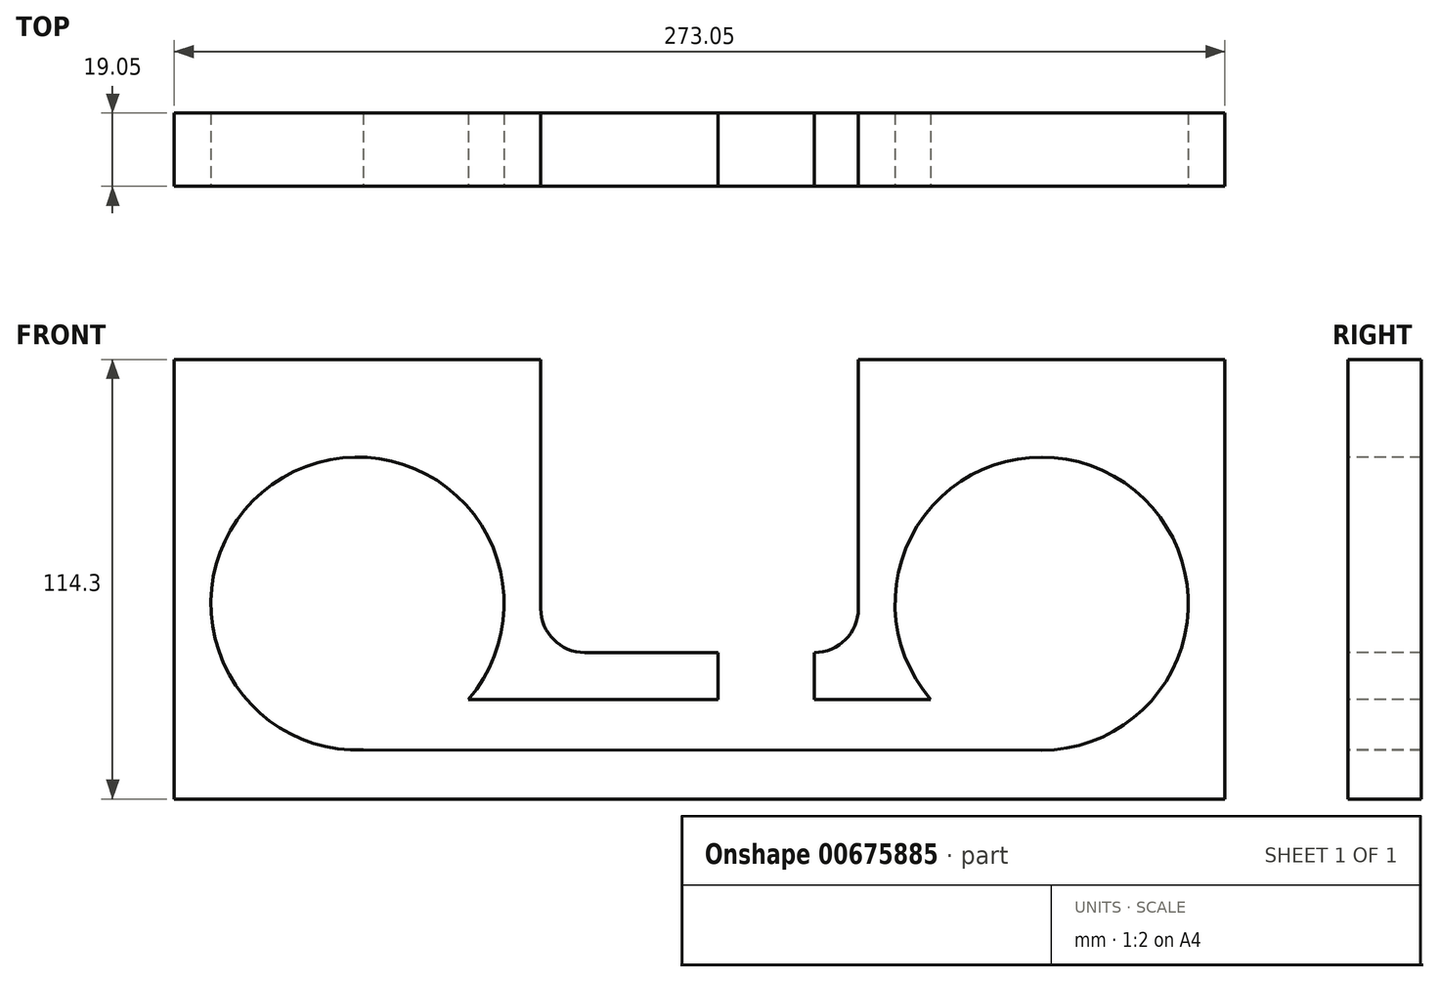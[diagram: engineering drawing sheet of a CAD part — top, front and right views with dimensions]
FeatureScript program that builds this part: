
annotation { "Feature Type Name" : "Feature", "Feature Type Description" : "" }
export const myFeature = defineFeature(function(context is Context, id is Id, definition is map)
    precondition{}
    {
        {
            var Q0;
            Q0=qCreatedBy(makeId("Front.planeOp"),FACE);
            var sketch = newSketch(context, id + "F0", { "sketchPlane" : qUnion([Q0])});
            skLineSegment(sketch, "E0.bottom", {"start": v(0, 0) * mm, "end": v(273.05, 0) * mm});
            skLineSegment(sketch, "E0.top", {"start": v(0, 114.3) * mm, "end": v(273.05, 114.3) * mm});
            skLineSegment(sketch, "E0.left", {"start": v(0, 0) * mm, "end": v(0, 114.3) * mm});
            skLineSegment(sketch, "E0.right", {"start": v(273.05, 0) * mm, "end": v(273.05, 114.3) * mm});
            skSolve(sketch);
        }
        {
            var Q0;
            Q0=makeQuery(id+"F0.imprint","IMPRINT",FACE,{"disambiguationData":[TD([[makeQuery(id+"F0.imprint","IMPRINT",EDGE,{"derivedFrom":sQuery(id+"F0.wireOp",EDGE,"E0.bottom")}),1.0]])]});
            extrude(context, id + "F1", {"entities" : qUnion([Q0]), "depth" : 19.05 * mm, "offsetDistance" : 25.4 * mm});
        }
        {
            var Q0;
            Q0=makeQuery(id+"F1.opExtrude","CAP_FACE",FACE,{"disambiguationData":[OSD([sQuery(id+"F0.wireOp",EDGE,"E0.bottom"),sQuery(id+"F0.wireOp",EDGE,"E0.top"),sQuery(id+"F0.wireOp",EDGE,"E0.left"),sQuery(id+"F0.wireOp",EDGE,"E0.right")])],"isStart":false});
            var sketch = newSketch(context, id + "F2", { "sketchPlane" : qUnion([Q0])});
            skCircle(sketch, "E1", {"center": v(47.63, 50.8) * mm, "radius": 38.1 * mm});
            skCircle(sketch, "E2", {"center": v(225.43, 50.8) * mm, "radius": 38.1 * mm});
            skSolve(sketch);
        }
        {
            var Q0;
            Q0=makeQuery(id+"F2.imprint","IMPRINT",FACE,{"disambiguationData":[TD([[makeQuery(id+"F2.imprint","IMPRINT",EDGE,{"derivedFrom":sQuery(id+"F2.wireOp",EDGE,"E1")}),1.0]])]});
            var Q1;
            Q1=makeQuery(id+"F2.imprint","IMPRINT",FACE,{"disambiguationData":[TD([[makeQuery(id+"F2.imprint","IMPRINT",EDGE,{"derivedFrom":sQuery(id+"F2.wireOp",EDGE,"E2")}),1.0]])]});
            extrude(context, id + "F3", {"entities" : qUnion([Q0, Q1]), "operationType" : NewBodyOperationType.REMOVE, "oppositeDirection" : true, "depth" : 25.4 * mm, "offsetDistance" : 25.4 * mm});
        }
        {
            var Q0;
            Q0=makeQuery(id+"F1.opExtrude","CAP_FACE",FACE,{"disambiguationData":[OSD([sQuery(id+"F0.wireOp",EDGE,"E0.bottom"),sQuery(id+"F0.wireOp",EDGE,"E0.top"),sQuery(id+"F0.wireOp",EDGE,"E0.left"),sQuery(id+"F0.wireOp",EDGE,"E0.right")])],"isStart":false});
            var sketch = newSketch(context, id + "F4", { "sketchPlane" : qUnion([Q0])});
            skLineSegment(sketch, "E3", {"start": v(95.25, 114.3) * mm, "end": v(95.25, 49.53) * mm});
            skLineSegment(sketch, "E4", {"start": v(106.68, 38.1) * mm, "end": v(166.37, 38.1) * mm});
            skLineSegment(sketch, "E5", {"start": v(177.8, 49.53) * mm, "end": v(177.8, 114.3) * mm});
            skPoint(sketch, "E6.visualSharp", {"position": v(95.25, 38.1) * mm});
            skArc(sketch, "E6.filletArc", {"start": v(95.25, 49.53) * mm, "mid": v(98.6, 41.45) * mm, "end": v(106.68, 38.1) * mm});
            skPoint(sketch, "E7.visualSharp", {"position": v(177.8, 38.1) * mm});
            skArc(sketch, "E7.filletArc", {"start": v(166.37, 38.1) * mm, "mid": v(174.45, 41.45) * mm, "end": v(177.8, 49.53) * mm});
            skSolve(sketch);
        }
        {
            var Q0;
            {var subQ1=sQuery(id+"F4.wireOp",EDGE,"E3");Q0=makeQuery(id+"F4.imprint","IMPRINT",FACE,{"disambiguationData":[TD([[makeQuery(id+"F4.imprint","IMPRINT",EDGE,{"derivedFrom":subQ1}),1.0]])]});}
            extrude(context, id + "F5", {"entities" : qUnion([Q0]), "operationType" : NewBodyOperationType.REMOVE, "oppositeDirection" : true, "depth" : 25.4 * mm, "offsetDistance" : 25.4 * mm});
        }
        {
            var Q0;
            Q0=makeQuery(id+"F1.opExtrude","CAP_FACE",FACE,{"disambiguationData":[OSD([sQuery(id+"F0.wireOp",EDGE,"E0.bottom"),sQuery(id+"F0.wireOp",EDGE,"E0.top"),sQuery(id+"F0.wireOp",EDGE,"E0.left"),sQuery(id+"F0.wireOp",EDGE,"E0.right")])],"isStart":false});
            var sketch = newSketch(context, id + "F6", { "sketchPlane" : qUnion([Q0])});
            skLineSegment(sketch, "E8", {"start": v(166.37, 38.1) * mm, "end": v(141.26, 38.1) * mm});
            skLineSegment(sketch, "E9", {"start": v(141.26, 38.1) * mm, "end": v(141.26, 25.87) * mm});
            skLineSegment(sketch, "E10", {"start": v(141.26, 25.87) * mm, "end": v(76.44, 25.87) * mm});
            skLineSegment(sketch, "E11", {"start": v(76.44, 25.87) * mm, "end": v(46.12, 12.73) * mm});
            skLineSegment(sketch, "E12", {"start": v(46.12, 12.73) * mm, "end": v(225.42, 12.7) * mm});
            skLineSegment(sketch, "E13", {"start": v(225.42, 12.7) * mm, "end": v(196.61, 25.87) * mm});
            skLineSegment(sketch, "E14", {"start": v(196.61, 25.87) * mm, "end": v(166.37, 25.87) * mm});
            skLineSegment(sketch, "E15", {"start": v(166.37, 25.87) * mm, "end": v(166.37, 38.1) * mm});
            skSolve(sketch);
        }
        {
            var Q0;
            Q0 = qSketchRegion(id + "F6", true);
            extrude(context, id + "F7", {"entities" : qUnion([Q0]), "operationType" : NewBodyOperationType.REMOVE, "oppositeDirection" : true, "depth" : 25.4 * mm, "offsetDistance" : 25.4 * mm});
        }
    });
